FCSTD DOCUMENT  (FreeCAD 0.21R33694 (Git))
Label: modelo_parametrico
License: All rights reserved
LicenseURL: https://en.wikipedia.org/wiki/All_rights_reserved
objects: Sketcher::SketchObject×7, PartDesign::Pad×4, PartDesign::Body×4, PartDesign::Plane×3, PartDesign::SubShapeBinder×3, PartDesign::Pocket×3, PartDesign::LinearPattern×2, Part::FeaturePython×2, Spreadsheet::Sheet×1, PartDesign::AdditiveSphere×1, PartDesign::MultiTransform×1, Part::Part2DObjectPython×1, Part::Extrusion×1, PartDesign::PolarPattern×1
note: 41 computed .brp shape members not serialized (recipe doc carries the construction recipe); baked Part::Feature solids carry a one-line shape summary decoded from their .brp

FEATURE [PartDesign::Plane] DatumPlane  label="ball plane"
  Length = 60
  MapMode = 2
  Placement = pos=(0,0,0.12) rot=(0,0,1;0rad)
  ResizeMode = 0
  Width = 60
  expr: .Placement.Base.z = Spreadsheet.plane_height
FEATURE [Spreadsheet::Sheet] Spreadsheet
  cells = A1='N; B1(ball_number)=42; A2='Length; B2(Length)=42.5; A3='ball distance; B3(ball_distance)=41; A4='radio; B4(radio)=0.3; A5='height; B5(height)=3.01; A6='plane height; B6(plane_height)=0.12
FEATURE [PartDesign::Plane] DatumPlane001  label="base capsule"
  Length = 60
  Placement = pos=(0,0,0.32) rot=(0,0,1;0rad)
  ResizeMode = 0
  Width = 60
  expr: .Placement.Base.z = Spreadsheet.plane_height + 0.2
FEATURE [PartDesign::Plane] DatumPlane002  label="base balls rectangle"
  Length = 60
  Placement = pos=(0,0,0.33) rot=(0,0,1;0rad)
  ResizeMode = 0
  Width = 60
  expr: .Placement.Base.z = Spreadsheet.plane_height + 0.21
FEATURE [Sketcher::SketchObject] Sketch
  FullyConstrained = true
  MapMode = 5
  Placement = pos=(0,0,0.33) rot=(0,0,1;0rad)
  Support = -> [DatumPlane002]
  expr: Constraints[10] = Spreadsheet.Length - 0.2
  sketch-geometry (4):
    g0: LineSegment StartX=-21.15 StartY=21.15 StartZ=0 EndX=21.15 EndY=21.15 EndZ=0
    g1: LineSegment StartX=21.15 StartY=21.15 StartZ=0 EndX=21.15 EndY=-21.15 EndZ=0
    g2: LineSegment StartX=21.15 StartY=-21.15 StartZ=0 EndX=-21.15 EndY=-21.15 EndZ=0
    g3: LineSegment StartX=-21.15 StartY=-21.15 StartZ=0 EndX=-21.15 EndY=21.15 EndZ=0
  constraints (11):
    c: Coincident(g0,g1)
    c: Coincident(g1,g2)
    c: Coincident(g2,g3)
    c: Coincident(g3,g0)
    c: Horizontal(g0)
    c: Horizontal(g2)
    c: Vertical(g1)
    c: Vertical(g3)
    c: Symmetric(g2,g0,g-1)
    c: Equal(g1,g0)
    c: DistanceY(g1,g1) = 42.3
FEATURE [PartDesign::Pad] Pad
  Direction = (0,0,1)
  Length = 0.1
  Length2 = 10
  Placement = pos=(0,0,0.33) rot=(0,0,1;0rad)
  Profile = -> Sketch
  ReferenceAxis = -> Sketch [N_Axis]
  Type = 0
FEATURE [PartDesign::AdditiveSphere] Sphere
  Angle1 = -90
  Angle2 = 90
  Angle3 = 360
  AttacherType = Attacher::AttachEngine3D
  AttachmentOffset = pos=(20.5,20.5,0) rot=(0,0,1;0rad)
  BaseFeature = -> Pad
  MapMode = 5
  Placement = pos=(20.5,20.5,0.12) rot=(0,0,1;0rad)
  Radius = 0.3
  Support = -> [DatumPlane]
  expr: .AttachmentOffset.Base.x = Spreadsheet.ball_distance / 2
  expr: .AttachmentOffset.Base.y = Spreadsheet.ball_distance / 2
  expr: Radius = Spreadsheet.radio
FEATURE [PartDesign::LinearPattern] LinearPattern
  Direction = -> X_Axis
  Length = 41
  Occurrences = 42
  Placement = pos=(20.5,20.5,0.12) rot=(0,0,1;0rad)
  Reversed = true
  expr: Length = Spreadsheet.ball_distance
  expr: Occurrences = Spreadsheet.ball_number
FEATURE [PartDesign::LinearPattern] LinearPattern001
  Direction = -> Y_Axis
  Length = 41
  Occurrences = 42
  Placement = pos=(20.5,20.5,0.12) rot=(0,0,1;0rad)
  Reversed = true
  expr: Length = Spreadsheet.ball_distance
  expr: Occurrences = Spreadsheet.ball_number
FEATURE [PartDesign::MultiTransform] MultiTransform
  BaseFeature = -> Sphere
  Originals = -> [Sphere]
  Placement = pos=(20.5,20.5,0.12) rot=(0,0,1;0rad)
  Transformations = -> [LinearPattern,LinearPattern001]
FEATURE [PartDesign::SubShapeBinder] Binder
  BindCopyOnChange = 0
  BindMode = 0
  ClaimChildren = false
  Context = -> Body001 [Binder.]
  Fuse = false
  MakeFace = true
  OffsetFill = false
  OffsetIntersection = false
  OffsetJoinType = 0
  OffsetOpenResult = false
  PartialLoad = false
  Relative = true
  Support = -> [Body[DatumPlane001.]]
  _Version = 2
FEATURE [Sketcher::SketchObject] Sketch001
  FullyConstrained = true
  MapMode = 5
  Placement = pos=(0,0,0.32) rot=(0,0,1;0rad)
  Support = -> [Binder]
  expr: Constraints[10] = Spreadsheet.Length
  sketch-geometry (4):
    g0: LineSegment StartX=-21.25 StartY=-21.25 StartZ=0 EndX=21.25 EndY=-21.25 EndZ=0
    g1: LineSegment StartX=21.25 StartY=-21.25 StartZ=0 EndX=21.25 EndY=21.25 EndZ=0
    g2: LineSegment StartX=21.25 StartY=21.25 StartZ=0 EndX=-21.25 EndY=21.25 EndZ=0
    g3: LineSegment StartX=-21.25 StartY=21.25 StartZ=0 EndX=-21.25 EndY=-21.25 EndZ=0
  constraints (11):
    c: Coincident(g0,g1)
    c: Coincident(g1,g2)
    c: Coincident(g2,g3)
    c: Coincident(g3,g0)
    c: Horizontal(g0)
    c: Horizontal(g2)
    c: Vertical(g1)
    c: Vertical(g3)
    c: Symmetric(g1,g0,g-1)
    c: Equal(g2,g1)
    c: DistanceY(g1,g1) = 42.5
FEATURE [PartDesign::Pad] Pad001
  Direction = (0,0,1)
  Length = 1.505
  Length2 = 10
  Profile = -> Sketch001
  ReferenceAxis = -> Sketch001 [N_Axis]
  Type = 0
  expr: Length = Spreadsheet.height / 2
FEATURE [PartDesign::Body] Body001  label="Cuerpo_inferior"
  Group = -> [Binder,DatumPlane001,Sketch001,Pad001]
  Origin = -> Origin001
  Tip = -> Pad001
FEATURE [PartDesign::SubShapeBinder] Binder001
  BindCopyOnChange = 0
  BindMode = 0
  ClaimChildren = false
  Context = -> Body002 [Binder001.]
  Fuse = false
  MakeFace = true
  OffsetFill = false
  OffsetIntersection = false
  OffsetJoinType = 0
  OffsetOpenResult = false
  PartialLoad = false
  Relative = true
  Support = -> [Body001[Pad001.Face6]]
  _Version = 2
FEATURE [Sketcher::SketchObject] Sketch002
  ExternalGeometry = -> [Binder001]
  FullyConstrained = true
  MapMode = 5
  Placement = pos=(0,0,1.825) rot=(0,0,1;0rad)
  expr: Constraints[10] = Spreadsheet.Length
  sketch-geometry (4):
    g0: LineSegment StartX=21.25 StartY=21.25 StartZ=0 EndX=-21.25 EndY=21.25 EndZ=0
    g1: LineSegment StartX=-21.25 StartY=21.25 StartZ=0 EndX=-21.25 EndY=-21.25 EndZ=0
    g2: LineSegment StartX=-21.25 StartY=-21.25 StartZ=0 EndX=21.25 EndY=-21.25 EndZ=0
    g3: LineSegment StartX=21.25 StartY=-21.25 StartZ=0 EndX=21.25 EndY=21.25 EndZ=0
  constraints (11):
    c: Coincident(g0,g1)
    c: Coincident(g1,g2)
    c: Coincident(g2,g3)
    c: Coincident(g3,g0)
    c: Horizontal(g0)
    c: Horizontal(g2)
    c: Vertical(g1)
    c: Vertical(g3)
    c: Symmetric(g0,g1,g-1)
    c: Equal(g3,g0)
    c: DistanceY(g3,g3) = 42.5
FEATURE [PartDesign::Pad] Pad002
  Direction = (0,0,1)
  Length = 1.505
  Length2 = 10
  Placement = pos=(0,0,1.825) rot=(0,0,1;0rad)
  Profile = -> Sketch002
  ReferenceAxis = -> Sketch002 [N_Axis]
  Type = 0
  expr: Length = Spreadsheet.height / 2
FEATURE [Part::Part2DObjectPython] Clone2D  label="Sketch003 (2D)"  # Draft 2D object (typed FeaturePython)
  Fuse = false
  Placement = pos=(-16.25,13.25,3.33) rot=(0,0,1;3.14159rad)
  Scale = (0.1,0.1,0.1)
  expr: .Placement.Base.x = -Spreadsheet.Length / 2 + 5
  expr: .Placement.Base.y = Spreadsheet.Length / 2 - 8
  expr: .Placement.Base.z = Spreadsheet.height + 0.32
FEATURE [Part::Extrusion] Extrude  label="logo"
  Base = -> Clone2D
  Dir = (0,0,1)
  DirMode = 2
  FaceMakerClass = Part::FaceMakerBullseye
  LengthFwd = 0.2
  LengthRev = 0
  Placement = pos=(1,-1,0) rot=(0,0,1;0rad)
  Solid = true
  Symmetric = false
FEATURE [Sketcher::SketchObject] Sketch003
  FullyConstrained = false
  MapMode = 5
  Placement = pos=(20.5,20.5,0.33) rot=(1,0,0;3.14159rad)
  Support = -> [MultiTransform]
  sketch-geometry (6):
    g0: LineSegment StartX=-43.6388 StartY=41.436 StartZ=0 EndX=-42.5276 EndY=41.436 EndZ=0
    g1: LineSegment StartX=-42.5276 StartY=41.436 StartZ=0 EndX=-42.5276 EndY=42.3899 EndZ=0
    g2: LineSegment StartX=-42.5276 StartY=42.3899 StartZ=0 EndX=-41.5286 EndY=42.3899 EndZ=0
    g3: LineSegment StartX=-41.5286 StartY=42.3899 StartZ=0 EndX=-41.5286 EndY=43.5121 EndZ=0
    g4: LineSegment StartX=-41.5286 StartY=43.5121 StartZ=0 EndX=-43.6388 EndY=43.5121 EndZ=0
    g5: LineSegment StartX=-43.6388 StartY=43.5121 StartZ=0 EndX=-43.6388 EndY=41.436 EndZ=0
  constraints (12):
    c: Horizontal(g0)
    c: Coincident(g0,g1)
    c: Vertical(g1)
    c: Coincident(g1,g2)
    c: Horizontal(g2)
    c: Coincident(g2,g3)
    c: Vertical(g3)
    c: Coincident(g3,g4)
    c: Horizontal(g4)
    c: Coincident(g4,g5)
    c: Coincident(g5,g0)
    c: Vertical(g5)
FEATURE [PartDesign::Pocket] Pocket
  BaseFeature = -> MultiTransform
  Direction = (0,0,1)
  Length = 5
  Length2 = 5
  Placement = pos=(20.5,20.5,0.12) rot=(0,0,1;0rad)
  Profile = -> Sketch003
  ReferenceAxis = -> Sketch003 [N_Axis]
  Reversed = true
  Type = 0
FEATURE [PartDesign::PolarPattern] PolarPattern
  Angle = 360
  Axis = -> Z_Axis
  BaseFeature = -> Pocket
  Occurrences = 4
  Originals = -> [Pocket]
  Placement = pos=(20.5,20.5,0.12) rot=(0,0,1;0rad)
FEATURE [PartDesign::Body] Body  label="bolas"
  Group = -> [DatumPlane,DatumPlane002,Sketch,Pad,Sphere,MultiTransform,LinearPattern,LinearPattern001,Sketch003,Pocket,PolarPattern]
  Origin = -> Origin
  Tip = -> PolarPattern
FEATURE [PartDesign::SubShapeBinder] Binder002
  BindCopyOnChange = 0
  BindMode = 0
  ClaimChildren = false
  Context = -> Body003 [Binder002.]
  Fuse = false
  MakeFace = true
  OffsetFill = false
  OffsetIntersection = false
  OffsetJoinType = 0
  OffsetOpenResult = false
  PartialLoad = false
  Relative = true
  Support = -> [Body002[Binder001.]]
  _Version = 2
FEATURE [Sketcher::SketchObject] Sketch004
  FullyConstrained = true
  MapMode = 5
  Placement = pos=(0,0,1.825) rot=(0,0,1;0rad)
  Support = -> [Binder002]
  expr: Constraints[10] = Spreadsheet.Length
  sketch-geometry (4):
    g0: LineSegment StartX=-21.25 StartY=-21.25 StartZ=0 EndX=21.25 EndY=-21.25 EndZ=0
    g1: LineSegment StartX=21.25 StartY=-21.25 StartZ=0 EndX=21.25 EndY=21.25 EndZ=0
    g2: LineSegment StartX=21.25 StartY=21.25 StartZ=0 EndX=-21.25 EndY=21.25 EndZ=0
    g3: LineSegment StartX=-21.25 StartY=21.25 StartZ=0 EndX=-21.25 EndY=-21.25 EndZ=0
  constraints (11):
    c: Coincident(g0,g1)
    c: Coincident(g1,g2)
    c: Coincident(g2,g3)
    c: Coincident(g3,g0)
    c: Horizontal(g0)
    c: Horizontal(g2)
    c: Vertical(g1)
    c: Vertical(g3)
    c: Equal(g1,g2)
    c: Symmetric(g1,g0,g-1)
    c: DistanceY(g1,g1) = 42.5
FEATURE [PartDesign::Pad] Pad003
  Direction = (0,0,1)
  Length = 1.505
  Length2 = 10
  Profile = -> Sketch004
  ReferenceAxis = -> Sketch004 [N_Axis]
  Type = 0
  expr: Length = Spreadsheet.height / 2
FEATURE [Sketcher::SketchObject] Sketch005
  ExternalGeometry = -> [Pad003]
  FullyConstrained = true
  MapMode = 5
  Placement = pos=(0,0,3.33) rot=(0,0,1;0rad)
  Support = -> [Pad003]
  sketch-geometry (1):
    g0: Circle CenterX=-19.25 CenterY=19.25 CenterZ=0 NormalX=0 NormalY=0 NormalZ=1 AngleXU=0 Radius=1
  constraints (3):
    c: DistanceY(g0,g-3) = 2
    c: DistanceX(g-3,g0) = 2
    c: Diameter(g0) = 2
FEATURE [PartDesign::Pocket] Pocket001
  BaseFeature = -> Pad003
  Direction = (0,0,-1)
  Length = 1
  Length2 = 5
  Profile = -> Sketch005
  ReferenceAxis = -> Sketch005 [N_Axis]
  Type = 0
FEATURE [PartDesign::Body] Body003  label="Cuerpo_superior_cuadrado_circulo"
  Group = -> [Binder002,Sketch004,Pad003,Sketch005,Pocket001]
  Origin = -> Origin003
  Tip = -> Pocket001
FEATURE [Sketcher::SketchObject] Sketch006
  ExternalGeometry = -> [Pad002]
  FullyConstrained = true
  MapMode = 5
  Placement = pos=(0,0,3.33) rot=(0,0,1;0rad)
  Support = -> [Pad002]
  sketch-geometry (4):
    g0: LineSegment StartX=-20.25 StartY=20.25 StartZ=0 EndX=-19.25 EndY=20.25 EndZ=0
    g1: LineSegment StartX=-19.25 StartY=20.25 StartZ=0 EndX=-19.25 EndY=19.25 EndZ=0
    g2: LineSegment StartX=-19.25 StartY=19.25 StartZ=0 EndX=-20.25 EndY=19.25 EndZ=0
    g3: LineSegment StartX=-20.25 StartY=19.25 StartZ=0 EndX=-20.25 EndY=20.25 EndZ=0
  constraints (12):
    c: Coincident(g0,g1)
    c: Coincident(g1,g2)
    c: Coincident(g2,g3)
    c: Coincident(g3,g0)
    c: Horizontal(g0)
    c: Horizontal(g2)
    c: Vertical(g1)
    c: Vertical(g3)
    c: DistanceX(g-3,g0) = 1
    c: DistanceY(g0,g-3) = 1
    c: Equal(g0,g1)
    c: DistanceY(g1,g1) = 1
FEATURE [PartDesign::Pocket] Pocket002
  BaseFeature = -> Pad002
  Direction = (0,0,-1)
  Length = 1
  Length2 = 5
  Placement = pos=(0,0,1.825) rot=(0,0,1;0rad)
  Profile = -> Sketch006
  ReferenceAxis = -> Sketch006 [N_Axis]
  Type = 0
FEATURE [PartDesign::Body] Body002  label="Cuerpo_superior_cuadrado_cuadrado"
  Group = -> [Binder001,Sketch002,Pad002,Sketch006,Pocket002]
  Origin = -> Origin002
  Tip = -> Pocket002
FEATURE [Part::FeaturePython] Clone  label="logo001"  # Draft clone (typed FeaturePython)
  AttacherType = Attacher::AttachEngine3D
  Fuse = false
  Objects = -> [Extrude]
  Placement = pos=(-6.33,6.36,0) rot=(0,0,1;0rad)
  Scale = (0.7,0.7,1)
FEATURE [Part::FeaturePython] Clone001  label="logo002"  # Draft clone (typed FeaturePython)
  AttacherType = Attacher::AttachEngine3D
  Fuse = false
  Objects = -> [Clone]
  Placement = pos=(-5.03,10.99,0) rot=(0,0,1;0rad)
  Scale = (0.6,0.6,1)
